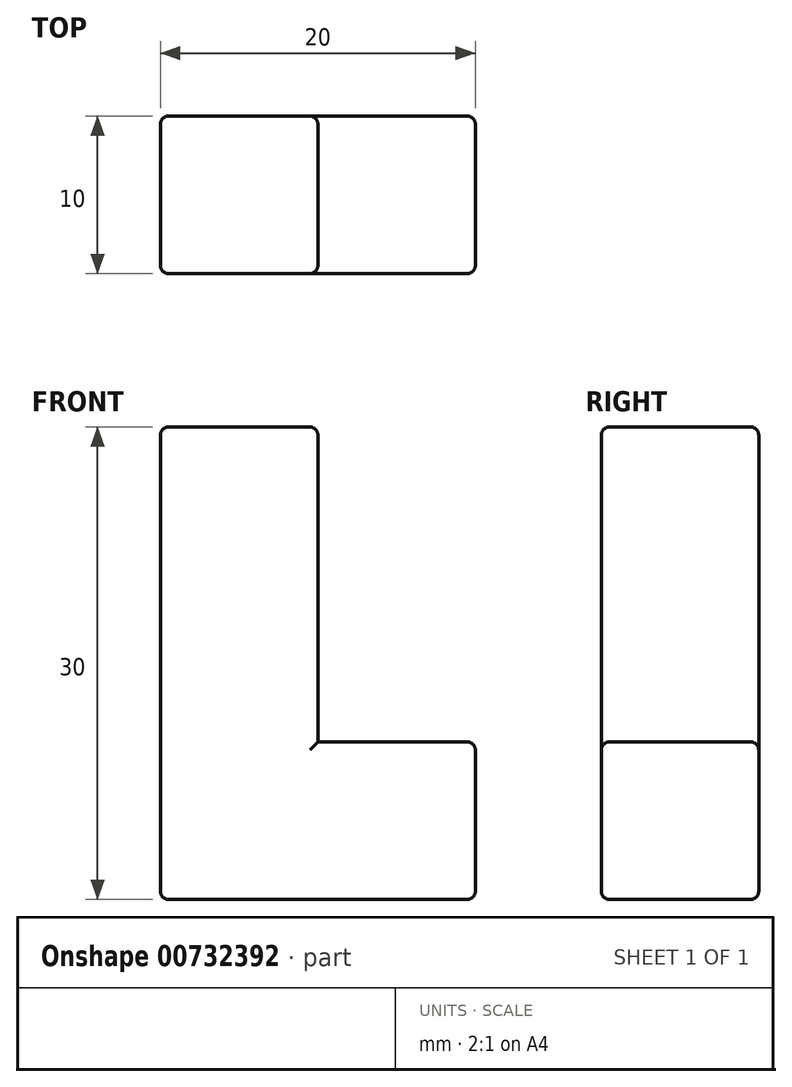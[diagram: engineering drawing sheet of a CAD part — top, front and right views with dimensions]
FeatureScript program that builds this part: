
annotation { "Feature Type Name" : "Feature", "Feature Type Description" : "" }
export const myFeature = defineFeature(function(context is Context, id is Id, definition is map)
    precondition{}
    {
        {
            var Q0;
            Q0=qCreatedBy(makeId("Front.planeOp"),FACE);
            var sketch = newSketch(context, id + "F0", { "sketchPlane" : qUnion([Q0])});
            skLineSegment(sketch, "E0.bottom", {"start": v(-5, 15) * mm, "end": v(5, 15) * mm});
            skLineSegment(sketch, "E0.top", {"start": v(-5, -15) * mm, "end": v(5, -15) * mm});
            skLineSegment(sketch, "E0.left", {"start": v(-5, 15) * mm, "end": v(-5, -15) * mm});
            skLineSegment(sketch, "E0.right", {"start": v(5, 15) * mm, "end": v(5, -15) * mm});
            skPoint(sketch, "E0.middle", {"position": v(0, 0) * mm});
            skLineSegment(sketch, "E1", {"start": v(5, -15) * mm, "end": v(15, -15) * mm});
            skLineSegment(sketch, "E2", {"start": v(15, -15) * mm, "end": v(15, -5) * mm});
            skLineSegment(sketch, "E3", {"start": v(15, -5) * mm, "end": v(5, -5) * mm});
            skSolve(sketch);
        }
        {
            var Q0;
            Q0 = qSketchRegion(id + "F0", true);
            extrude(context, id + "F1", {"entities" : qUnion([Q0]), "depth" : 10 * mm, "offsetDistance" : 25 * mm});
        }
        {
            var Q0;
            Q0=makeQuery(id+"F1.opExtrude","CAP_FACE",FACE,{"disambiguationData":[OSD([sQuery(id+"F0.wireOp",EDGE,"E0.bottom"),sQuery(id+"F0.wireOp",EDGE,"E0.top"),sQuery(id+"F0.wireOp",EDGE,"E0.left"),sQuery(id+"F0.wireOp",EDGE,"E0.right"),sQuery(id+"F0.wireOp",EDGE,"E1"),sQuery(id+"F0.wireOp",EDGE,"E2"),sQuery(id+"F0.wireOp",EDGE,"E3")])],"isStart":false});
            var Q1;
            Q1=makeQuery(id+"F1.opExtrude","CAP_FACE",FACE,{"disambiguationData":[OSD([sQuery(id+"F0.wireOp",EDGE,"E0.bottom"),sQuery(id+"F0.wireOp",EDGE,"E0.top"),sQuery(id+"F0.wireOp",EDGE,"E0.left"),sQuery(id+"F0.wireOp",EDGE,"E0.right"),sQuery(id+"F0.wireOp",EDGE,"E1"),sQuery(id+"F0.wireOp",EDGE,"E2"),sQuery(id+"F0.wireOp",EDGE,"E3")])],"isStart":true});
            fillet(context, id + "F2", {"entities" : qUnion([Q0, Q1]), "radius" : 0.5 * mm, "tangentPropagation" : true, "allowEdgeOverflow" : false});
        }
        {
            var Q0;
            Q0=makeQuery(id+"F1.opExtrude","SWEPT_FACE",FACE,{"disambiguationData":[OSD([sQuery(id+"F0.wireOp",EDGE,"E0.top"),sQuery(id+"F0.wireOp",EDGE,"E1")])]});
            var Q1;
            Q1=makeQuery(id+"F1.opExtrude","SWEPT_FACE",FACE,{"disambiguationData":[OSD([sQuery(id+"F0.wireOp",EDGE,"E0.bottom")])]});
            var Q2;
            Q2=makeQuery(id+"F1.opExtrude","SWEPT_FACE",FACE,{"disambiguationData":[OSD([sQuery(id+"F0.wireOp",EDGE,"E2")])]});
            fillet(context, id + "F3", {"entities" : qUnion([Q0, Q1, Q2]), "radius" : 0.5 * mm, "tangentPropagation" : true, "allowEdgeOverflow" : false});
        }
    });
